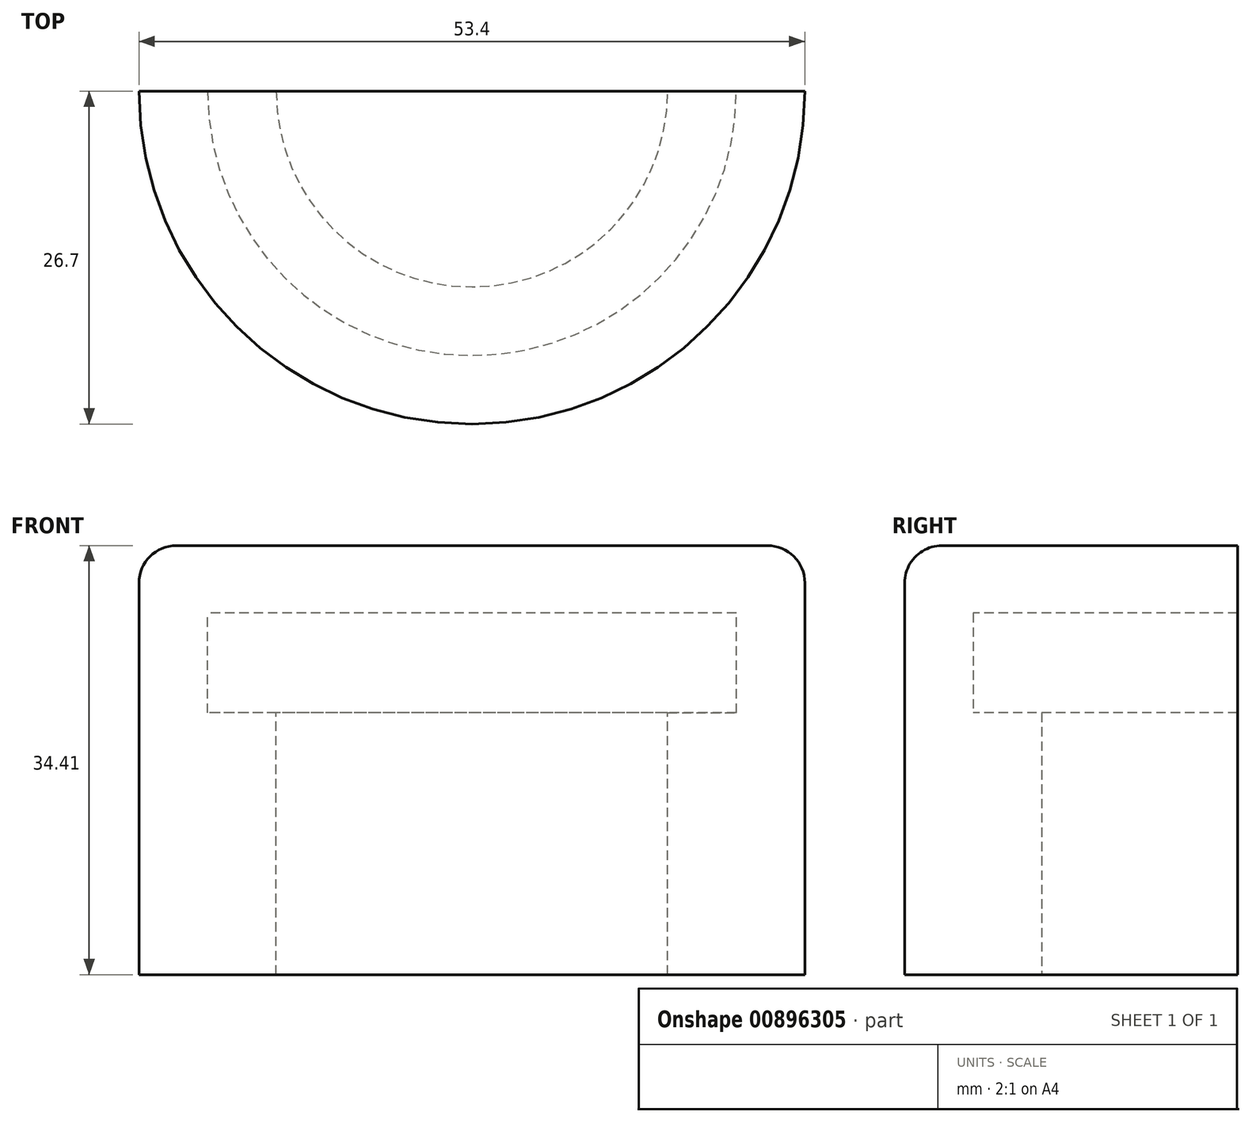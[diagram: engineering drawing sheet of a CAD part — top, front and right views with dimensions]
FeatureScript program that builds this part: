
annotation { "Feature Type Name" : "Feature", "Feature Type Description" : "" }
export const myFeature = defineFeature(function(context is Context, id is Id, definition is map)
    precondition{}
    {
        {
            var Q0;
            Q0=qCreatedBy(makeId("Front.planeOp"),FACE);
            var sketch = newSketch(context, id + "F0", { "sketchPlane" : qUnion([Q0])});
            skPoint(sketch, "E0.end.orphan", {"position": v(-0.06, 30.6) * mm});
            skLineSegment(sketch, "E1", {"start": v(-15.76, 0.2) * mm, "end": v(-15.76, 21.2) * mm});
            skLineSegment(sketch, "E2", {"start": v(-15.76, 21.2) * mm, "end": v(-21.26, 21.2) * mm});
            skLineSegment(sketch, "E3", {"start": v(-21.26, 21.2) * mm, "end": v(-21.26, 29.2) * mm});
            skLineSegment(sketch, "E4", {"start": v(-26.76, 29.12) * mm, "end": v(-26.76, 34.62) * mm});
            skLineSegment(sketch, "E5", {"start": v(-26.76, 34.62) * mm, "end": v(-0.06, 34.62) * mm});
            skLineSegment(sketch, "E6", {"start": v(-21.26, 29.2) * mm, "end": v(-0.06, 29.2) * mm});
            skLineSegment(sketch, "E7", {"start": v(-0.06, 29.2) * mm, "end": v(-0.06, 34.62) * mm});
            skLineSegment(sketch, "E8", {"start": v(-0.06, 0.12) * mm, "end": v(-0.06, 6.75) * mm});
            skLineSegment(sketch, "E9", {"start": v(-15.76, 0.2) * mm, "end": v(-26.76, 0.2) * mm});
            skLineSegment(sketch, "E10", {"start": v(-26.76, 29.12) * mm, "end": v(-26.76, 23.88) * mm});
            skLineSegment(sketch, "E11", {"start": v(-26.76, 8.08) * mm, "end": v(-26.76, 0.2) * mm});
            skLineSegment(sketch, "E12", {"start": v(-26.76, 23.88) * mm, "end": v(-26.76, 8.08) * mm});
            skSolve(sketch);
        }
        {
            var Q0;
            Q0=makeQuery(id+"F0.imprint","IMPRINT",FACE,{"disambiguationData":[TD([[makeQuery(id+"F0.imprint","IMPRINT",EDGE,{"derivedFrom":sQuery(id+"F0.wireOp",EDGE,"E1")}),1.0]])]});
            var Q1;
            Q1=sQuery(id+"F0.wireOp",EDGE,"E8");
            revolve(context, id + "F1", {"surfaceOperationType" : NewSurfaceOperationType.NEW, "entities" : qUnion([Q0]), "axis" : qUnion([Q1]), "revolveType" : RevolveType.ONE_DIRECTION, "angle" : 180 * degree});
        }
        {
            var Q0;
            Q0=makeQuery(id+"F1.opRevolve","SWEPT_EDGE",EDGE,{"disambiguationData":[OSD([sQuery(id+"F0.wireOp",EDGE,"E4"),sQuery(id+"F0.wireOp",EDGE,"E5")])]});
            fillet(context, id + "F2", {"entities" : qUnion([Q0]), "radius" : 3 * mm, "tangentPropagation" : true, "allowEdgeOverflow" : false});
        }
    });
